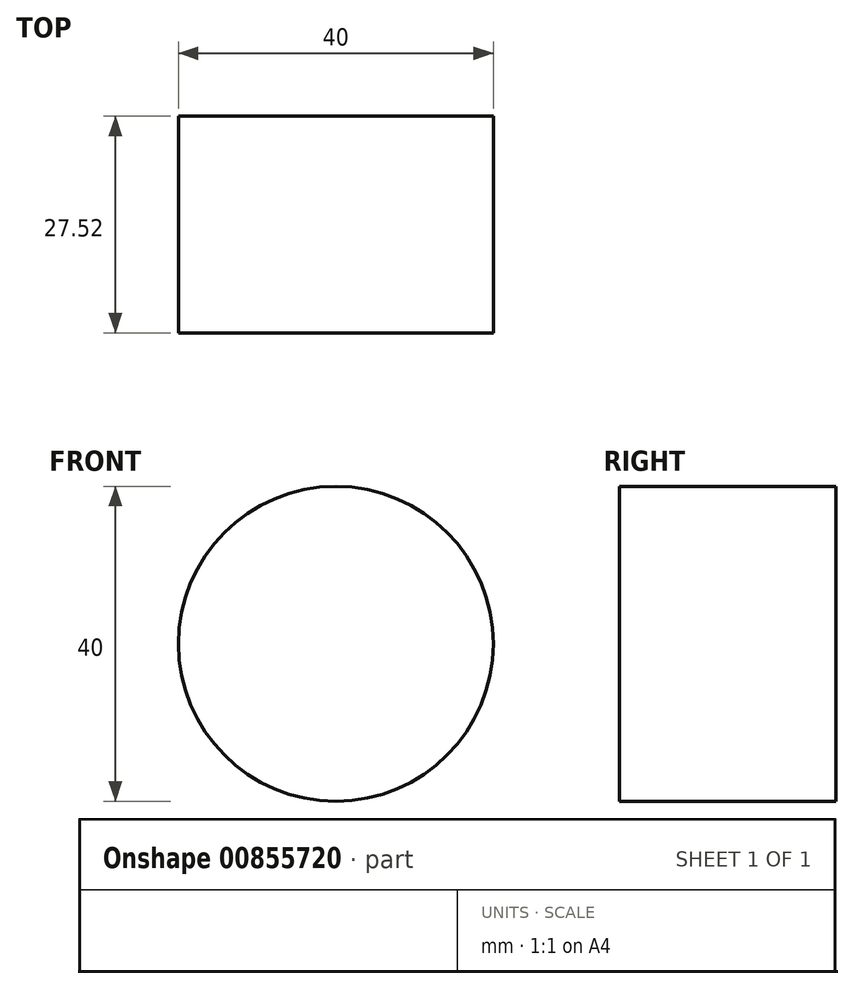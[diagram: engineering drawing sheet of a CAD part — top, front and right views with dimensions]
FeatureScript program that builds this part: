
annotation { "Feature Type Name" : "Feature", "Feature Type Description" : "" }
export const myFeature = defineFeature(function(context is Context, id is Id, definition is map)
    precondition{}
    {
        {
            var Q0;
            Q0=qCreatedBy(makeId("Front.planeOp"),FACE);
            var sketch = newSketch(context, id + "F0", { "sketchPlane" : qUnion([Q0])});
            skCircle(sketch, "E0", {"center": v(0, 0) * mm, "radius": 20 * mm});
            skSolve(sketch);
        }
        {
            var Q0;
            Q0=qCreatedBy(makeId("Right.planeOp"),FACE);
            var sketch = newSketch(context, id + "F1", { "sketchPlane" : qUnion([Q0])});
            skLineSegment(sketch, "E1", {"start": v(0, 0) * mm, "end": v(27.52, 0) * mm});
            skArc(sketch, "E2", {"start": v(27.52, 0) * mm, "mid": v(56.07, -7.22) * mm, "end": v(77.73, -27.15) * mm, "construction": true});
            skSolve(sketch);
        }
        {
            var Q0;
            Q0=makeQuery(id+"F0.imprint","IMPRINT",FACE,{"disambiguationData":[TD([[makeQuery(id+"F0.imprint","IMPRINT",EDGE,{"derivedFrom":sQuery(id+"F0.wireOp",EDGE,"E0")}),1.0]])]});
            var Q1;
            Q1=sQuery(id+"F1.wireOp",EDGE,"E1");
            sweep(context, id + "F2", {"profiles" : qUnion([Q0]), "path" : qUnion([Q1])});
        }
    });
